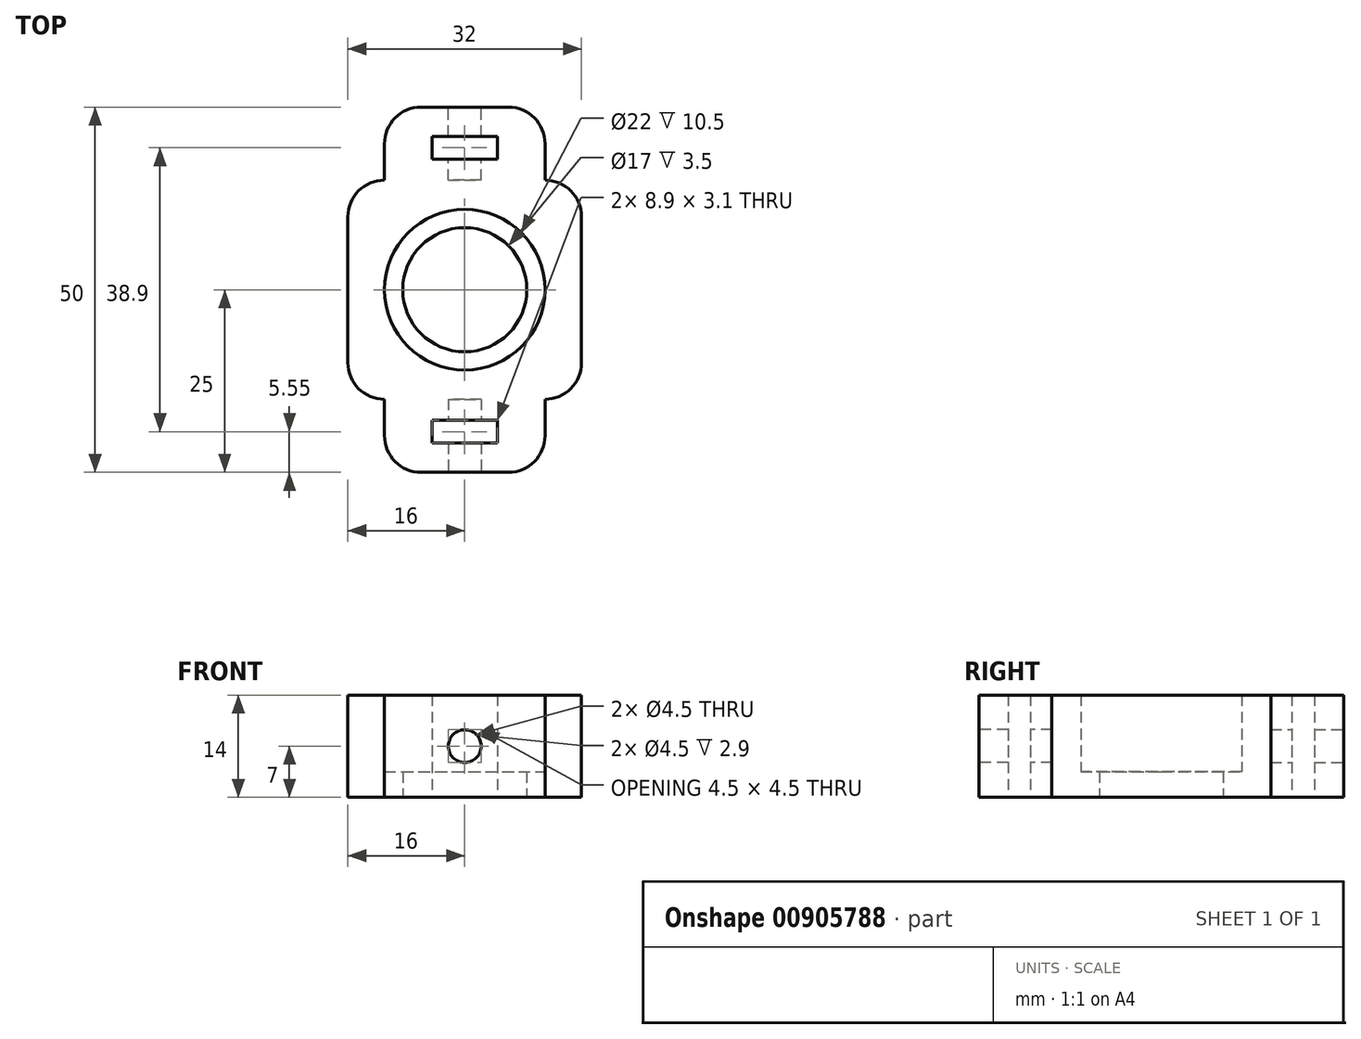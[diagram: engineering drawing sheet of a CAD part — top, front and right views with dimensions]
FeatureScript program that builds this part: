
annotation { "Feature Type Name" : "Feature", "Feature Type Description" : "" }
export const myFeature = defineFeature(function(context is Context, id is Id, definition is map)
    precondition{}
    {
        {
            var Q0;
            Q0=qCreatedBy(makeId("Top.planeOp"),FACE);
            var sketch = newSketch(context, id + "F0", { "sketchPlane" : qUnion([Q0])});
            skCircle(sketch, "E0", {"center": v(0, 0) * mm, "radius": 11 * mm});
            skLineSegment(sketch, "E1.bottom", {"start": v(11, -15) * mm, "end": v(11, -15) * mm});
            skLineSegment(sketch, "E1.left", {"start": v(-16, -10) * mm, "end": v(-16, 10) * mm});
            skLineSegment(sketch, "E1.right", {"start": v(16, -10) * mm, "end": v(16, 10) * mm});
            skLineSegment(sketch, "E2.bottom", {"start": v(-6, -25) * mm, "end": v(6, -25) * mm});
            skLineSegment(sketch, "E2.top", {"start": v(-6, 25) * mm, "end": v(6, 25) * mm});
            skLineSegment(sketch, "E2.left", {"start": v(-11, -20) * mm, "end": v(-11, -15) * mm});
            skLineSegment(sketch, "E2.right", {"start": v(11, -20) * mm, "end": v(11, -15) * mm});
            skPoint(sketch, "E3.visualSharp", {"position": v(-11, 25) * mm});
            skArc(sketch, "E3.filletArc", {"start": v(-6, 25) * mm, "mid": v(-9.54, 23.54) * mm, "end": v(-11, 20) * mm});
            skPoint(sketch, "E4.visualSharp", {"position": v(11, 25) * mm});
            skArc(sketch, "E4.filletArc", {"start": v(11, 20) * mm, "mid": v(9.54, 23.54) * mm, "end": v(6, 25) * mm});
            skPoint(sketch, "E5.visualSharp", {"position": v(11, -25) * mm});
            skArc(sketch, "E5.filletArc", {"start": v(6, -25) * mm, "mid": v(9.54, -23.54) * mm, "end": v(11, -20) * mm});
            skPoint(sketch, "E6.visualSharp", {"position": v(-11, -25) * mm});
            skArc(sketch, "E6.filletArc", {"start": v(-11, -20) * mm, "mid": v(-9.54, -23.54) * mm, "end": v(-6, -25) * mm});
            skPoint(sketch, "E7.visualSharp", {"position": v(-16, -15) * mm});
            skArc(sketch, "E7.filletArc", {"start": v(-16, -10) * mm, "mid": v(-14.54, -13.54) * mm, "end": v(-11, -15) * mm});
            skPoint(sketch, "E8.visualSharp", {"position": v(-16, 15) * mm});
            skArc(sketch, "E8.filletArc", {"start": v(-11, 15) * mm, "mid": v(-14.54, 13.54) * mm, "end": v(-16, 10) * mm});
            skPoint(sketch, "E9.visualSharp", {"position": v(16, 15) * mm});
            skArc(sketch, "E9.filletArc", {"start": v(16, 10) * mm, "mid": v(14.54, 13.54) * mm, "end": v(11, 15) * mm});
            skLineSegment(sketch, "E10.trimOffspring", {"start": v(-11, 15) * mm, "end": v(-11, 20) * mm});
            skLineSegment(sketch, "E11.trimOffspring", {"start": v(11, 15) * mm, "end": v(11, 20) * mm});
            skPoint(sketch, "E12.visualSharp", {"position": v(16, -15) * mm});
            skArc(sketch, "E12.filletArc", {"start": v(11, -15) * mm, "mid": v(14.54, -13.54) * mm, "end": v(16, -10) * mm});
            skLineSegment(sketch, "E13.bottom", {"start": v(-4.45, 17.9) * mm, "end": v(4.45, 17.9) * mm});
            skLineSegment(sketch, "E13.top", {"start": v(-4.45, 21) * mm, "end": v(4.45, 21) * mm});
            skLineSegment(sketch, "E13.left", {"start": v(-4.45, 17.9) * mm, "end": v(-4.45, 21) * mm});
            skLineSegment(sketch, "E13.right", {"start": v(4.45, 17.9) * mm, "end": v(4.45, 21) * mm});
            skPoint(sketch, "E13.middle", {"position": v(0, 19.45) * mm});
            skPoint(sketch, "E13.middle.positionSnap0", {"position": v(0, 25) * mm});
            skPoint(sketch, "E13.centerSnap0", {"position": v(0, 25) * mm});
            skLineSegment(sketch, "E14.MirrorCS", {"start": v(-4.45, -17.9) * mm, "end": v(4.45, -17.9) * mm});
            skLineSegment(sketch, "E15.MirrorCS", {"start": v(-4.45, -21) * mm, "end": v(4.45, -21) * mm});
            skLineSegment(sketch, "E16.MirrorCS", {"start": v(-4.45, -17.9) * mm, "end": v(-4.45, -21) * mm});
            skLineSegment(sketch, "E17.MirrorCS", {"start": v(4.45, -17.9) * mm, "end": v(4.45, -21) * mm});
            skSolve(sketch);
        }
        {
            var Q0;
            Q0=makeQuery(id+"F0.imprint","IMPRINT",FACE,{"disambiguationData":[TD([[makeQuery(id+"F0.imprint","IMPRINT",EDGE,{"derivedFrom":sQuery(id+"F0.wireOp",EDGE,"E0")}),-1.0]])]});
            extrude(context, id + "F1", {"entities" : qUnion([Q0]), "depth" : 7 * mm, "offsetDistance" : 25 * mm, "hasSecondDirection" : true, "secondDirectionOppositeDirection" : true, "secondDirectionDepth" : 7 * mm});
        }
        {
            var Q0;
            Q0=makeQuery(id+"F1.opExtrude","SWEPT_FACE",FACE,{"disambiguationData":[OSD([sQuery(id+"F0.wireOp",EDGE,"E2.bottom")])]});
            var sketch = newSketch(context, id + "F2", { "sketchPlane" : qUnion([Q0])});
            skCircle(sketch, "E18", {"center": v(0, 0) * mm, "radius": 2.25 * mm});
            skSolve(sketch);
        }
        {
            var Q0;
            Q0=makeQuery(id+"F2.imprint","IMPRINT",FACE,{"disambiguationData":[TD([[makeQuery(id+"F2.imprint","IMPRINT",EDGE,{"derivedFrom":sQuery(id+"F2.wireOp",EDGE,"E18")}),1.0]])]});
            extrude(context, id + "F3", {"entities" : qUnion([Q0]), "operationType" : NewBodyOperationType.REMOVE, "oppositeDirection" : true, "depth" : 10 * mm, "offsetDistance" : 25 * mm});
        }
        {
            var Q0;
            Q0=makeQuery(id+"F1.opExtrude","SWEPT_FACE",FACE,{"disambiguationData":[OSD([sQuery(id+"F0.wireOp",EDGE,"E2.top")])]});
            var sketch = newSketch(context, id + "F4", { "sketchPlane" : qUnion([Q0])});
            skCircle(sketch, "E19", {"center": v(0, 0) * mm, "radius": 2.25 * mm});
            skSolve(sketch);
        }
        {
            var Q0;
            Q0=makeQuery(id+"F4.imprint","IMPRINT",FACE,{"disambiguationData":[TD([[makeQuery(id+"F4.imprint","IMPRINT",EDGE,{"derivedFrom":sQuery(id+"F4.wireOp",EDGE,"E19")}),1.0]])]});
            extrude(context, id + "F5", {"entities" : qUnion([Q0]), "operationType" : NewBodyOperationType.REMOVE, "oppositeDirection" : true, "depth" : 10 * mm, "offsetDistance" : 25 * mm});
        }
        {
            var Q0;
            Q0=makeQuery(id+"F1.opExtrude","CAP_FACE",FACE,{"disambiguationData":[OSD([sQuery(id+"F0.wireOp",EDGE,"E0"),sQuery(id+"F0.wireOp",EDGE,"E1.left"),sQuery(id+"F0.wireOp",EDGE,"E1.right"),sQuery(id+"F0.wireOp",EDGE,"E2.bottom"),sQuery(id+"F0.wireOp",EDGE,"E2.top"),sQuery(id+"F0.wireOp",EDGE,"E2.left"),sQuery(id+"F0.wireOp",EDGE,"E2.right"),sQuery(id+"F0.wireOp",EDGE,"E3.filletArc"),sQuery(id+"F0.wireOp",EDGE,"E4.filletArc"),sQuery(id+"F0.wireOp",EDGE,"E5.filletArc"),sQuery(id+"F0.wireOp",EDGE,"E6.filletArc"),sQuery(id+"F0.wireOp",EDGE,"E7.filletArc"),sQuery(id+"F0.wireOp",EDGE,"E8.filletArc"),sQuery(id+"F0.wireOp",EDGE,"E9.filletArc"),sQuery(id+"F0.wireOp",EDGE,"E10.trimOffspring"),sQuery(id+"F0.wireOp",EDGE,"E11.trimOffspring"),sQuery(id+"F0.wireOp",EDGE,"E12.filletArc"),sQuery(id+"F0.wireOp",EDGE,"E13.bottom"),sQuery(id+"F0.wireOp",EDGE,"E13.top"),sQuery(id+"F0.wireOp",EDGE,"E13.left"),sQuery(id+"F0.wireOp",EDGE,"E13.right"),sQuery(id+"F0.wireOp",EDGE,"E14.MirrorCS"),sQuery(id+"F0.wireOp",EDGE,"E15.MirrorCS"),sQuery(id+"F0.wireOp",EDGE,"E16.MirrorCS"),sQuery(id+"F0.wireOp",EDGE,"E17.MirrorCS")])],"isStart":true});
            var sketch = newSketch(context, id + "F6", { "sketchPlane" : qUnion([Q0])});
            skCircle(sketch, "E20", {"center": v(0, 0) * mm, "radius": 11.25 * mm});
            skCircle(sketch, "E21", {"center": v(0, 0) * mm, "radius": 8.5 * mm});
            skSolve(sketch);
        }
        {
            var Q0;
            Q0 = qSketchRegion(id + "F6", true);
            extrude(context, id + "F7", {"entities" : qUnion([Q0]), "operationType" : NewBodyOperationType.ADD, "oppositeDirection" : true, "depth" : 3.5 * mm, "offsetDistance" : 25 * mm});
        }
    });
